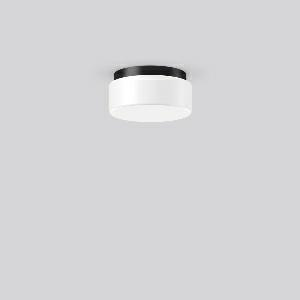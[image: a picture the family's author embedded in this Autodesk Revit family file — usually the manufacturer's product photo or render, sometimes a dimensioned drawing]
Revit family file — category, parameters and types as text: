
# Revit family: kreis_21101_003_5cd7
name_source: partatom
category: Lighting Fixtures
units: mm (PartAtom-declared; Revit-internal decimal feet)

## family parameters
Cut with Voids When Loaded = No
Host = Face
Light Source = No
Part Type = Normal
Room Calculation Point = No
Round Connector Dimension = Use Diameter
Shared = No

## types (1)
- KREIS (1 x QA60/clear E27, 915 lm, 57 W, 3000)
    Apparent Load = 57 VA
    CIE Flux Codes = 34 63 85 71 62
    Color Rendering = 90
    Color Temperature = 3000
    Default Elevation = 1800 mm
    Description = Series: KREIS
Round surface-mounted luminaire in classic design. Base: plastic. Opal glass: mouth-blown, satin finish. Diffuser fastening: spring system. Suitable for Ceiling mounting, Wall (surface). IP 43 ceiling mounting, IP 44 wall mounting. 
Colour: black
Diameter: 230 mm
Height: 110 mm
Lamp: A60
Number of lamps: 1
Wattage: 75 W
Socket: E27
System power: 57 W
Rated luminous flux: 570 lm
Luminous efficiency: 10 lm/W
Control gear: Converter not necessary
Protection class: II
Type of protection: IP 43
    Height = 110 mm
    Lamp = 1 x QA60/clear E27
    Lamp Light Flux = 915 lm
    Lamp Power = 57 W
    Lamp count = 1
    Length = 230 mm
    Lifetime = 3000 h
    Luminous efficacy = 10 lm/W
    Manufacturer = RZB
    ModVariant = No
    Model = 21101.003
    Mounting Place = Wall, Ceiling
    Mounting Type = Surface mounted
    Number of Poles = 1
    OnlyDefault = Yes
    Power Factor = 1
    Product Name = KREIS
    Product group = Surface mounted ceiling and wall luminaires
    ProductGroupID = 305
    Protection Class = Protection class II
    Protection Degree = IP 43
    RLX_Detail_Level = 1
    RLX_Emergency_Light_Flux = 0 lm
    RLX_Emergency_Type = 0
    RLX_Emergency_Type_DB = No
    RlxData = <blob elided: 11861 chars, md5=e4fdb533>
    Socket = E27
    Standby Power = 0 W
    System Light Flux = 565 lm
    System Power = 57 W
    Type Comments = Product without accessories
    Type Image = 21101.003.jpg
    URL = http://relux.com
    VarID = ---
    Voltage = 230 V
    Voltage Range = 220-240 V
    Weight = 0.00 kg
    Width = 0 mm  [stored 0 ft]

note: [stored X ft] marks values corroborated as IEEE doubles in the binary element streams (Revit-internal decimal feet)

## geometry (parser evidence)
native form markers: Sweep x11
no freeform markers — native parametric forms only
